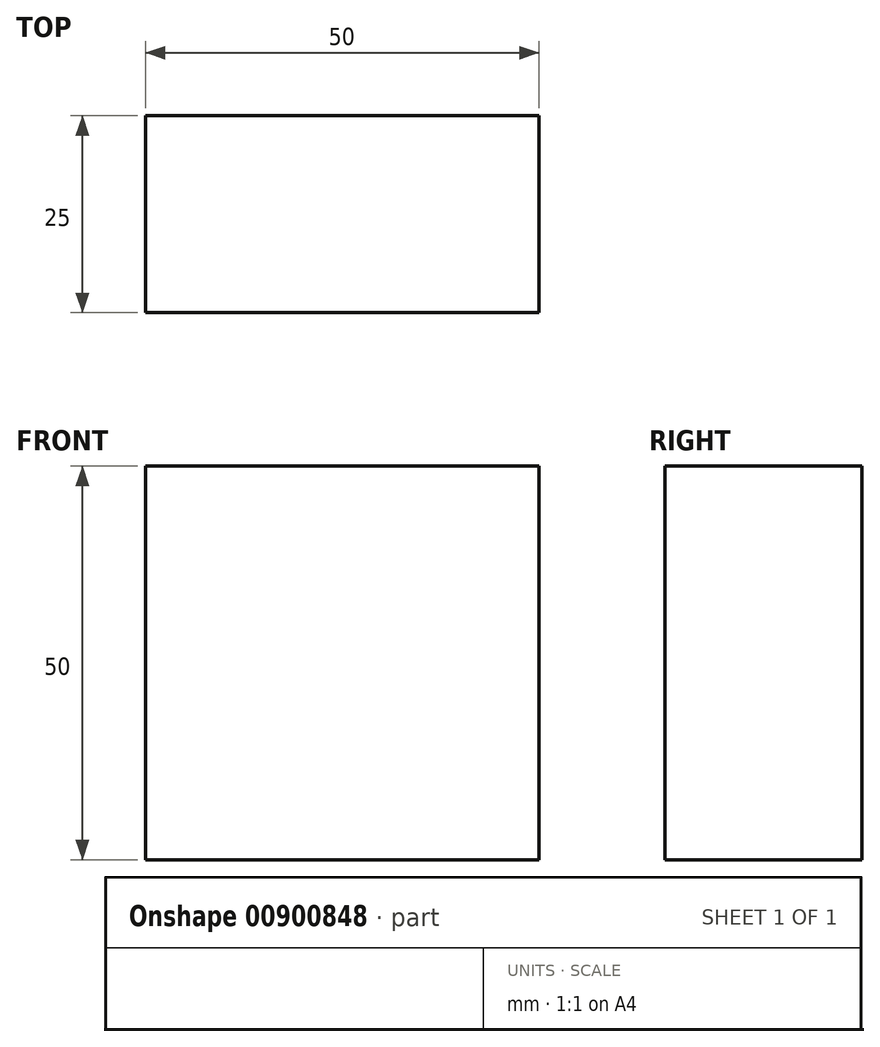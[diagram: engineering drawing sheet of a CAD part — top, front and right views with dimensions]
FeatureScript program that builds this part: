
annotation { "Feature Type Name" : "Feature", "Feature Type Description" : "" }
export const myFeature = defineFeature(function(context is Context, id is Id, definition is map)
    precondition{}
    {
        {
            var Q0;
            Q0=qCreatedBy(makeId("Front.planeOp"),FACE);
            var sketch = newSketch(context, id + "F0", { "sketchPlane" : qUnion([Q0])});
            skLineSegment(sketch, "E0.bottom", {"start": v(-25, 25) * mm, "end": v(25, 25) * mm});
            skLineSegment(sketch, "E0.top", {"start": v(-25, -25) * mm, "end": v(25, -25) * mm});
            skLineSegment(sketch, "E0.left", {"start": v(-25, 25) * mm, "end": v(-25, -25) * mm});
            skLineSegment(sketch, "E0.right", {"start": v(25, 25) * mm, "end": v(25, -25) * mm});
            skSolve(sketch);
        }
        {
            var Q0;
            Q0 = qSketchRegion(id + "F0", true);
            extrude(context, id + "F1", {"entities" : qUnion([Q0]), "depth" : 25 * mm, "offsetDistance" : 25 * mm});
        }
    });
